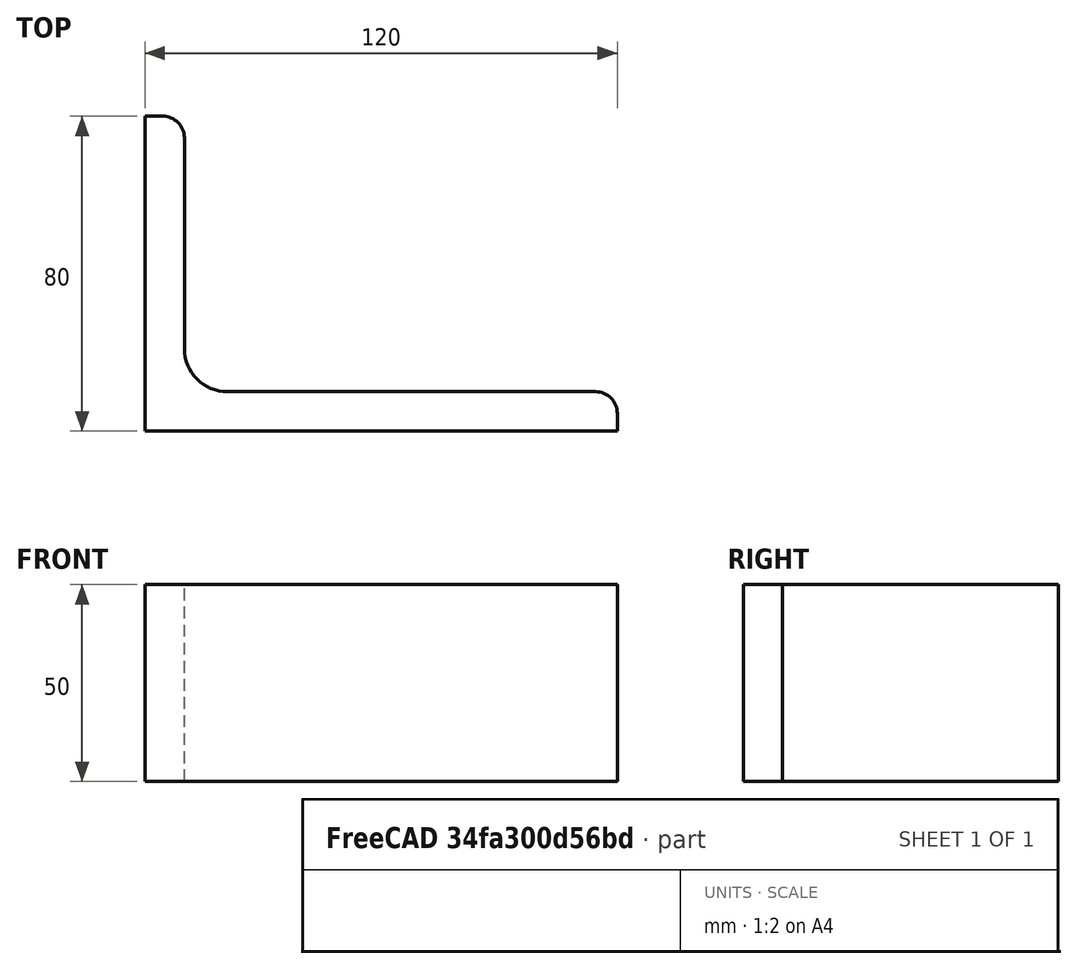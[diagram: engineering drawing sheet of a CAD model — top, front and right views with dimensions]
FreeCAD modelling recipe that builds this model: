
FCSTD DOCUMENT  (FreeCAD 0.15R4671 (Git))
Label: Angle Bar 120x80x10 EN10056 S235JR
License: All rights reserved
LicenseURL: http://en.wikipedia.org/wiki/All_rights_reserved
objects: Sketcher::SketchObject×1, Part::Extrusion×1
note: 2 computed .brp shape members not serialized (recipe doc carries the construction recipe); baked Part::Feature solids carry a one-line shape summary decoded from their .brp

FEATURE [Sketcher::SketchObject] Sketch
  sketch-geometry (9):
    g0: LineSegment StartX=0 StartY=0 StartZ=0 EndX=120 EndY=0 EndZ=0
    g1: LineSegment StartX=120 StartY=0 StartZ=0 EndX=120 EndY=4.5 EndZ=0
    g2: LineSegment StartX=114.5 StartY=10 StartZ=0 EndX=21 EndY=10 EndZ=0
    g3: LineSegment StartX=0 StartY=0 StartZ=0 EndX=0 EndY=80 EndZ=0
    g4: LineSegment StartX=0 StartY=80 StartZ=0 EndX=4.5 EndY=80 EndZ=0
    g5: LineSegment StartX=10 StartY=74.5 StartZ=0 EndX=10 EndY=21 EndZ=0
    g6: ArcOfCircle CenterX=21 CenterY=21 CenterZ=0 NormalX=0 NormalY=0 NormalZ=1 Radius=11 StartAngle=3.14159 EndAngle=4.71239
    g7: ArcOfCircle CenterX=4.5 CenterY=74.5 CenterZ=0 NormalX=0 NormalY=0 NormalZ=1 Radius=5.5 StartAngle=0 EndAngle=1.5708
    g8: ArcOfCircle CenterX=114.5 CenterY=4.5 CenterZ=0 NormalX=0 NormalY=0 NormalZ=1 Radius=5.5 StartAngle=0 EndAngle=1.5708
  constraints (23):
    c: Coincident(g0,g-1)
    c: Horizontal(g0)
    c: Coincident(g1,g0)
    c: Vertical(g1)
    c: Horizontal(g2)
    c: Coincident(g3,g-1)
    c: Vertical(g3)
    c: Coincident(g4,g3)
    c: Horizontal(g4)
    c: Vertical(g5)
    c: Tangent(g5,g6) = -1.5708
    c: Tangent(g2,g6) = 1.5708
    c: Tangent(g4,g7) = 1.5708
    c: Tangent(g5,g7) = 1.5708
    c: Tangent(g2,g8) = -1.5708
    c: Tangent(g1,g8) = -1.5708
    c: DistanceX(g0) = 120
    c: DistanceY(g3) = 80
    c: DistanceY(g0,g2) = 10
    c: DistanceX(g3,g5) = 10
    c: Radius(g6) = 11
    c: Radius(g8) = 5.5
    c: Radius(g7) = 5.5
FEATURE [Part::Extrusion] Extrude  label="Angle Bar 120x80x10 EN10056 S235JR"
  Base = -> Sketch
  Dir = (0,0,50)
  Solid = true
